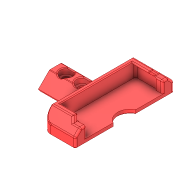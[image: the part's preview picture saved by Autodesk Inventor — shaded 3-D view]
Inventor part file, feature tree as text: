
AUTODESK INVENTOR PART (.ipt)
format: ipt  version: 2021 (Build 250183000, 183)  size: 562,688 bytes
history: native  units: mm
features: projected_geometry x5, fillet x4, other x4, direct_edit x3, extrude x2, sketch x2, chamfer x1
ambient origin geometry x8: Origin, YZ Plane, XZ Plane, XY Plane, X Axis, Y Axis, Z Axis, Center Point
bodies: Volumenkörper1 (feature_tree), Body1 (feature_tree)
feature tree (21):
  extrude  "Extrusion1"  Depth=10.0mm
  extrude  "Extrusion4"  Depth=1.0mm TaperAngle=45.0deg
  direct_edit  "Direktbearbeitung2"
  direct_edit  "Direktbearbeitung3"
  direct_edit  "Direktbearbeitung4"
  chamfer  "Fase1"  Distance=0.5mm
  fillet  "Rundung7"  Radius=0.55mm
  fillet  "Rundung8"  Radius=1.0mm
  fillet  "Rundung9"  Radius=1.0mm
  fillet  "Rundung10"  [1 undecoded]
  sketch  "Skizze1"  dims[d0=10.0mm d1=0.0mm d17=1.75mm]
  projected_geometry  "Projizierte Kontur1"
  projected_geometry  "Projizierte Kontur2"
  projected_geometry  "Projizierte Kontur3"
  projected_geometry  "Projizierte Kontur4"
  sketch  "Skizze4"  dims[d18=0.0mm d19=0.0mm d20=1.75mm d21=2.0mm d22=45.0deg d23=0.5mm d24=0.55mm d25=1.0mm d26=1.0mm]
  projected_geometry  "Projizierte Kontur12"
  other  "Löschen4"
  other  "Löschen5"
  other  "Löschen6"
  other  "Löschen7"
note: 1 required parameter value undecoded (feature->parameter linkage not recoverable at this tier; creation-order binding heuristic only, values carry confidence <= 0.55)
